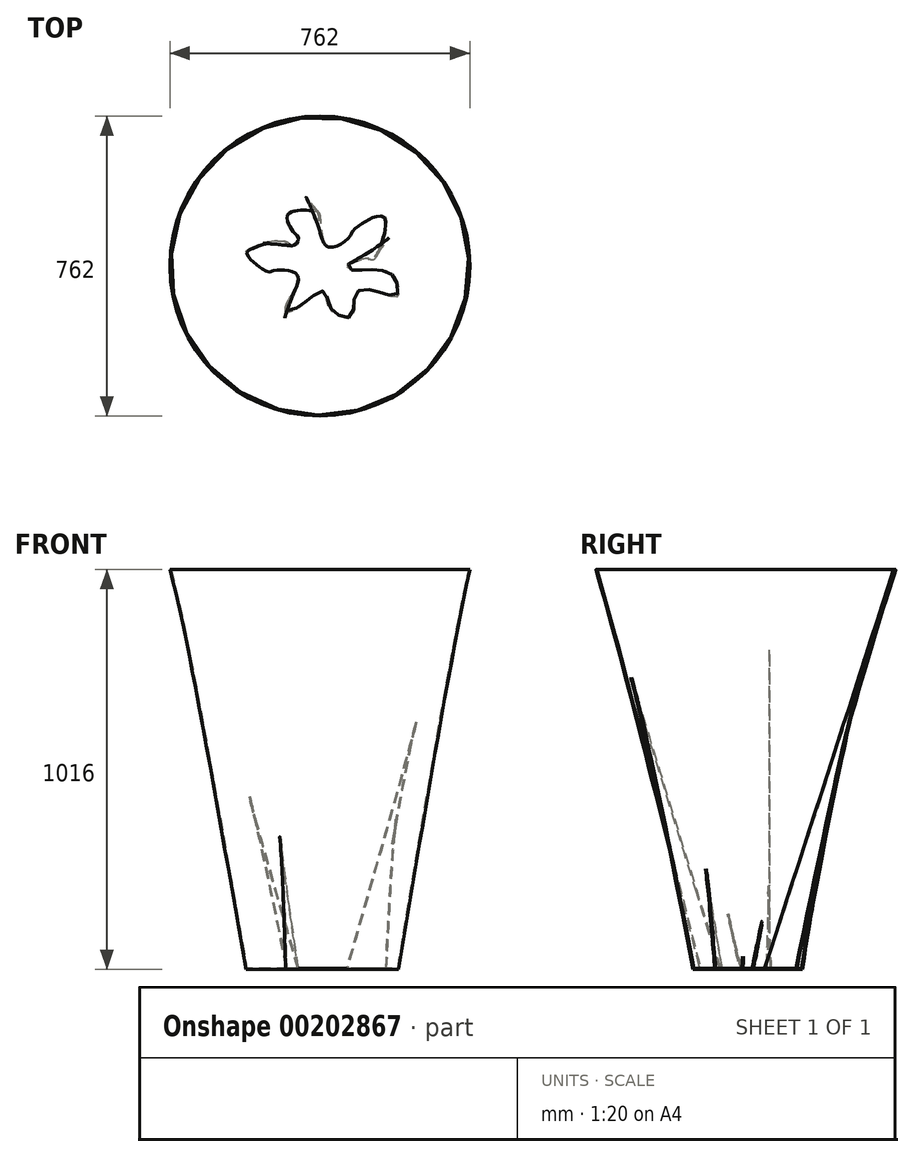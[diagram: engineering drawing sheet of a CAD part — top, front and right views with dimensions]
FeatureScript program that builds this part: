
annotation { "Feature Type Name" : "Feature", "Feature Type Description" : "" }
export const myFeature = defineFeature(function(context is Context, id is Id, definition is map)
    precondition{}
    {
        {
            var Q0;
            Q0=qCreatedBy(makeId("Top.planeOp"),FACE);
            cPlane(context, id + "F0", {"entities" : qUnion([Q0]), "cplaneType" : CPlaneType.OFFSET, "offset" : 1016 * mm, "width" : 152.4 * mm, "height" : 152.4 * mm});
        }
        {
            var Q0;
            Q0=qCreatedBy(makeId("Top.planeOp"),FACE);
            var sketch = newSketch(context, id + "F1", { "sketchPlane" : qUnion([Q0])});
            skFitSpline(sketch, "E0", {"points": [v(8.02, -64.85) * mm, v(-72.98, -116.24) * mm, v(-86.92, -104.05) * mm, v(-57.3, -26.53) * mm, v(-114.79, -13.47) * mm, v(-133.95, -16.08) * mm, v(-186.2, 27.47) * mm, v(-178.37, 44.02) * mm, v(-88.66, 64.05) * mm, v(-70.37, 53.6) * mm, v(-55.56, 67.54) * mm, v(-66.88, 83.21) * mm, v(-82.56, 132.86) * mm, v(-13.75, 141.57) * mm, v(0, 128.5) * mm, v(20.22, 50.99) * mm, v(75.09, 76.25) * mm, v(84.67, 92.8) * mm, v(164.8, 125.9) * mm, v(138.67, 17.89) * mm, v(122.12, 17.02) * mm, v(69.86, 0) * mm, v(81.19, -7.37) * mm, v(181.35, -16.95) * mm, v(199.64, -70.08) * mm, v(188.32, -78.8) * mm, v(97.73, -64.85) * mm, v(81.19, -129.3) * mm, v(24.57, -106.66) * mm, v(8.02, -64.85) * mm]});
            skSolve(sketch);
        }
        {
            var Q0;
            Q0=qCreatedBy(id+"F0.planeOp",FACE);
            var sketch = newSketch(context, id + "F2", { "sketchPlane" : qUnion([Q0])});
            skCircle(sketch, "E1", {"center": v(0, 0) * mm, "radius": 381 * mm});
            skSolve(sketch);
        }
        {
            var Q0;
            Q0=makeQuery(id+"F1.imprint","IMPRINT",FACE,{"disambiguationData":[TD([[makeQuery(id+"F1.imprint","IMPRINT",EDGE,{"derivedFrom":sQuery(id+"F1.wireOp",EDGE,"E0")}),-1.0]])]});
            var Q1;
            Q1=makeQuery(id+"F2.imprint","IMPRINT",FACE,{"disambiguationData":[TD([[makeQuery(id+"F2.imprint","IMPRINT",EDGE,{"derivedFrom":sQuery(id+"F2.wireOp",EDGE,"E1")}),1.0]])]});
            loft(context, id + "F3", {"sheetProfilesArray" : [{ "sheetProfileEntities" : qUnion([Q0]) }, { "sheetProfileEntities" : qUnion([Q1]) }]});
        }
        {
            var Q0;
            Q0=makeQuery(id+"F3.opLoft","CAP_FACE",FACE,{"disambiguationData":[OSD([makeQuery(id+"F2.imprint","IMPRINT",FACE,{"disambiguationData":[TD([[makeQuery(id+"F2.imprint","IMPRINT",EDGE,{"derivedFrom":sQuery(id+"F2.wireOp",EDGE,"E1")}),1.0]])]})])],"isStart":true});
            shell(context, id + "F4", {"entities" : qUnion([Q0]), "thickness" : 2.54 * mm});
        }
    });
